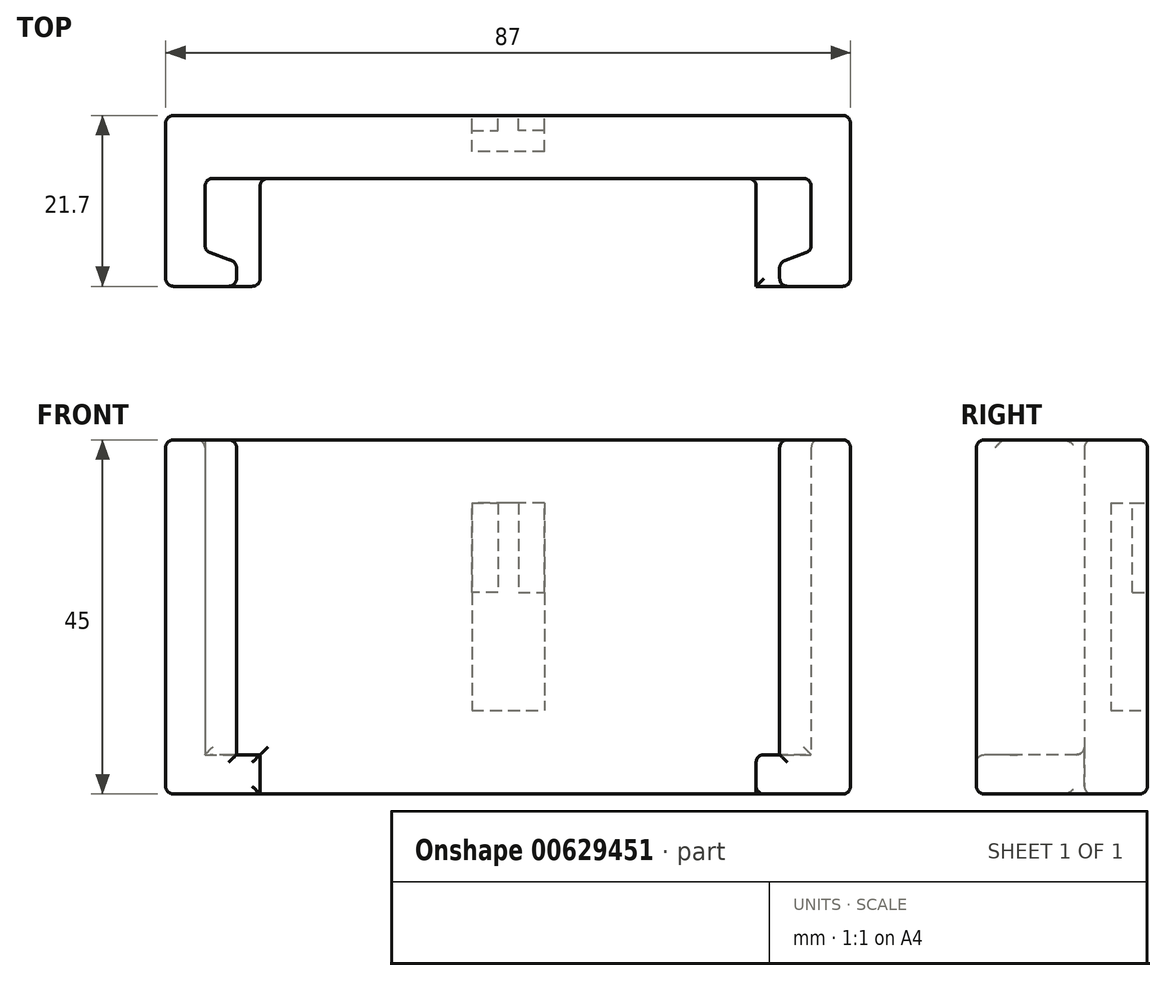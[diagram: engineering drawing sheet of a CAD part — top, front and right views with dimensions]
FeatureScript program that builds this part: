
annotation { "Feature Type Name" : "Feature", "Feature Type Description" : "" }
export const myFeature = defineFeature(function(context is Context, id is Id, definition is map)
    precondition{}
    {
        {
            var Q0;
            Q0=qCreatedBy(makeId("Top.planeOp"),FACE);
            var sketch = newSketch(context, id + "F0", { "sketchPlane" : qUnion([Q0])});
            skLineSegment(sketch, "E0", {"start": v(0, 0) * mm, "end": v(87, 0) * mm});
            skLineSegment(sketch, "E1", {"start": v(87, 0) * mm, "end": v(87, -21.7) * mm});
            skLineSegment(sketch, "E2", {"start": v(87, -21.7) * mm, "end": v(0, -21.7) * mm});
            skLineSegment(sketch, "E3", {"start": v(0, -21.7) * mm, "end": v(0, 0) * mm});
            skSolve(sketch);
        }
        {
            var Q0;
            Q0 = qSketchRegion(id + "F0", true);
            extrude(context, id + "F1", {"entities" : qUnion([Q0]), "depth" : 5 * mm, "offsetDistance" : 25 * mm});
        }
        {
            var Q0;
            Q0=makeQuery(id+"F1.opExtrude","CAP_FACE",FACE,{"disambiguationData":[OSD([sQuery(id+"F0.wireOp",EDGE,"E0"),sQuery(id+"F0.wireOp",EDGE,"E1"),sQuery(id+"F0.wireOp",EDGE,"E2"),sQuery(id+"F0.wireOp",EDGE,"E3")])],"isStart":false});
            var sketch = newSketch(context, id + "F2", { "sketchPlane" : qUnion([Q0])});
            skLineSegment(sketch, "E4", {"start": v(0, 0) * mm, "end": v(0, -21.7) * mm});
            skLineSegment(sketch, "E5", {"start": v(0, -21.7) * mm, "end": v(9, -21.7) * mm});
            skLineSegment(sketch, "E6", {"start": v(9, -21.7) * mm, "end": v(9, -18.66) * mm});
            skLineSegment(sketch, "E7", {"start": v(9, -18.66) * mm, "end": v(5, -17.2) * mm});
            skLineSegment(sketch, "E8", {"start": v(5, -17.2) * mm, "end": v(5, -8) * mm});
            skLineSegment(sketch, "E9", {"start": v(5, -8) * mm, "end": v(82, -8) * mm});
            skLineSegment(sketch, "E10", {"start": v(82, -8) * mm, "end": v(82, -17.2) * mm});
            skLineSegment(sketch, "E11", {"start": v(82, -17.2) * mm, "end": v(78, -18.66) * mm});
            skLineSegment(sketch, "E12", {"start": v(78, -18.66) * mm, "end": v(78, -21.7) * mm});
            skLineSegment(sketch, "E13", {"start": v(78, -21.7) * mm, "end": v(87, -21.7) * mm});
            skLineSegment(sketch, "E14", {"start": v(87, -21.7) * mm, "end": v(87, 0) * mm});
            skLineSegment(sketch, "E15", {"start": v(87, 0) * mm, "end": v(0, 0) * mm});
            skSolve(sketch);
        }
        {
            var Q0;
            Q0=makeQuery(id+"F2.imprint","IMPRINT",FACE,{"disambiguationData":[TD([[makeQuery(id+"F2.imprint","IMPRINT",EDGE,{"derivedFrom":sQuery(id+"F2.wireOp",EDGE,"E4")}),-1.0]])]});
            extrude(context, id + "F3", {"entities" : qUnion([Q0]), "operationType" : NewBodyOperationType.ADD, "depth" : 40 * mm, "offsetDistance" : 25 * mm});
        }
        {
            var Q0;
            Q0=makeQuery(id+"F3.boolean.opBoolean","MERGE",FACE,{"derivedFrom":[makeQuery(id+"F1.opExtrude","SWEPT_FACE",FACE,{"disambiguationData":[OSD([sQuery(id+"F0.wireOp",EDGE,"E0")])]}),makeQuery(id+"F3.opExtrude","SWEPT_FACE",FACE,{"disambiguationData":[OSD([sQuery(id+"F2.wireOp",EDGE,"E15")])]})]});
            var sketch = newSketch(context, id + "F4", { "sketchPlane" : qUnion([Q0])});
            skLineSegment(sketch, "E16", {"start": v(-43.5, 45) * mm, "end": v(-43.5, 0) * mm, "construction": true});
            skLineSegment(sketch, "E17", {"start": v(-43.5, 37) * mm, "end": v(-44.8, 37) * mm});
            skLineSegment(sketch, "E18", {"start": v(-44.8, 37) * mm, "end": v(-44.8, 25.6) * mm});
            skLineSegment(sketch, "E19", {"start": v(-44.8, 25.6) * mm, "end": v(-48.1, 25.6) * mm});
            skLineSegment(sketch, "E20", {"start": v(-48.1, 25.6) * mm, "end": v(-48.1, 10.6) * mm});
            skLineSegment(sketch, "E21", {"start": v(-48.1, 10.6) * mm, "end": v(-43.5, 10.6) * mm});
            skLineSegment(sketch, "E22", {"start": v(-43.5, 10.6) * mm, "end": v(-43.5, 37) * mm});
            skLineSegment(sketch, "E23", {"start": v(-43.5, 37) * mm, "end": v(-42.2, 37) * mm});
            skLineSegment(sketch, "E24", {"start": v(-42.2, 37) * mm, "end": v(-42.2, 25.6) * mm});
            skLineSegment(sketch, "E25", {"start": v(-42.2, 25.6) * mm, "end": v(-38.9, 25.6) * mm});
            skLineSegment(sketch, "E26", {"start": v(-38.9, 25.6) * mm, "end": v(-38.9, 10.6) * mm});
            skLineSegment(sketch, "E27", {"start": v(-38.9, 10.6) * mm, "end": v(-43.5, 10.6) * mm});
            skSolve(sketch);
        }
        {
            var Q0;
            Q0=makeQuery(id+"F4.imprint","IMPRINT",FACE,{"disambiguationData":[TD([[makeQuery(id+"F4.imprint","IMPRINT",EDGE,{"derivedFrom":sQuery(id+"F4.wireOp",EDGE,"E22")}),-1.0]])]});
            var Q1;
            Q1=makeQuery(id+"F4.imprint","IMPRINT",FACE,{"disambiguationData":[TD([[makeQuery(id+"F4.imprint","IMPRINT",EDGE,{"derivedFrom":sQuery(id+"F4.wireOp",EDGE,"E17")}),1.0]])]});
            extrude(context, id + "F5", {"entities" : qUnion([Q0, Q1]), "operationType" : NewBodyOperationType.REMOVE, "oppositeDirection" : true, "depth" : 4.6 * mm, "offsetDistance" : 25 * mm});
        }
        {
            var Q0;
            Q0=makeQuery(id+"F5.boolean.opBoolean","COPY",FACE,{"derivedFrom":makeQuery(id+"F5.opExtrude","SWEPT_FACE",FACE,{"disambiguationData":[OSD([sQuery(id+"F4.wireOp",EDGE,"E24")])]})});
            var sketch = newSketch(context, id + "F6", { "sketchPlane" : qUnion([Q0])});
            skLineSegment(sketch, "E28", {"start": v(-1.9, 37) * mm, "end": v(0, 37) * mm});
            skLineSegment(sketch, "E29", {"start": v(0, 37) * mm, "end": v(0, 25.6) * mm});
            skLineSegment(sketch, "E30", {"start": v(0, 25.6) * mm, "end": v(-1.9, 25.6) * mm});
            skLineSegment(sketch, "E31", {"start": v(-1.9, 25.6) * mm, "end": v(-1.9, 37) * mm});
            skLineSegment(sketch, "E32.bottom", {"start": v(-1.9, 25.6) * mm, "end": v(-4.6, 25.6) * mm});
            skLineSegment(sketch, "E32.top", {"start": v(-1.9, 37) * mm, "end": v(-4.6, 37) * mm});
            skLineSegment(sketch, "E32.right", {"start": v(-4.6, 25.6) * mm, "end": v(-4.6, 37) * mm});
            skSolve(sketch);
        }
        {
            var Q0;
            Q0=makeQuery(id+"F6.imprint","IMPRINT",FACE,{"disambiguationData":[TD([[makeQuery(id+"F6.imprint","IMPRINT",EDGE,{"derivedFrom":sQuery(id+"F6.wireOp",EDGE,"E32.bottom")}),1.0]])]});
            extrude(context, id + "F7", {"entities" : qUnion([Q0]), "operationType" : NewBodyOperationType.REMOVE, "oppositeDirection" : true, "depth" : 3.3 * mm, "offsetDistance" : 25 * mm});
        }
        {
            var Q0;
            Q0=makeQuery(id+"F5.boolean.opBoolean","COPY",FACE,{"derivedFrom":makeQuery(id+"F5.opExtrude","SWEPT_FACE",FACE,{"disambiguationData":[OSD([sQuery(id+"F4.wireOp",EDGE,"E18")])]})});
            var sketch = newSketch(context, id + "F8", { "sketchPlane" : qUnion([Q0])});
            skLineSegment(sketch, "E33", {"start": v(1.9, 37) * mm, "end": v(0, 37) * mm});
            skLineSegment(sketch, "E34", {"start": v(0, 37) * mm, "end": v(0, 25.6) * mm});
            skLineSegment(sketch, "E35", {"start": v(0, 25.6) * mm, "end": v(1.9, 25.6) * mm});
            skLineSegment(sketch, "E36", {"start": v(1.9, 25.6) * mm, "end": v(1.9, 37) * mm});
            skLineSegment(sketch, "E37.bottom", {"start": v(4.6, 37) * mm, "end": v(1.9, 37) * mm});
            skLineSegment(sketch, "E37.top", {"start": v(4.6, 25.6) * mm, "end": v(1.9, 25.6) * mm});
            skLineSegment(sketch, "E37.left", {"start": v(4.6, 37) * mm, "end": v(4.6, 25.6) * mm});
            skLineSegment(sketch, "E37.right", {"start": v(1.9, 37) * mm, "end": v(1.9, 25.6) * mm});
            skSolve(sketch);
        }
        {
            var Q0;
            Q0=makeQuery(id+"F8.imprint","IMPRINT",FACE,{"disambiguationData":[TD([[makeQuery(id+"F8.imprint","IMPRINT",EDGE,{"derivedFrom":sQuery(id+"F8.wireOp",EDGE,"E37.bottom")}),1.0]])]});
            extrude(context, id + "F9", {"entities" : qUnion([Q0]), "operationType" : NewBodyOperationType.REMOVE, "oppositeDirection" : true, "depth" : 3.3 * mm, "offsetDistance" : 25 * mm});
        }
        {
            var Q0;
            Q0=makeQuery(id+"F3.boolean.opBoolean","MERGE",FACE,{"derivedFrom":[makeQuery(id+"F1.opExtrude","SWEPT_FACE",FACE,{"disambiguationData":[OSD([sQuery(id+"F0.wireOp",EDGE,"E2")])]}),makeQuery(id+"F3.opExtrude","SWEPT_FACE",FACE,{"disambiguationData":[OSD([sQuery(id+"F2.wireOp",EDGE,"E5")])]}),makeQuery(id+"F3.opExtrude","SWEPT_FACE",FACE,{"disambiguationData":[OSD([sQuery(id+"F2.wireOp",EDGE,"E13")])]})]});
            var sketch = newSketch(context, id + "F10", { "sketchPlane" : qUnion([Q0])});
            skLineSegment(sketch, "E38", {"start": v(12, 5) * mm, "end": v(12, 0) * mm});
            skLineSegment(sketch, "E39", {"start": v(12, 0) * mm, "end": v(75, 0) * mm});
            skLineSegment(sketch, "E40", {"start": v(75, 0) * mm, "end": v(75, 5) * mm});
            skLineSegment(sketch, "E41", {"start": v(75, 5) * mm, "end": v(12, 5) * mm});
            skSolve(sketch);
        }
        {
            var Q0;
            Q0=makeQuery(id+"F10.imprint","IMPRINT",FACE,{"disambiguationData":[TD([[makeQuery(id+"F10.imprint","IMPRINT",EDGE,{"derivedFrom":sQuery(id+"F10.wireOp",EDGE,"E38")}),1.0]])]});
            extrude(context, id + "F11", {"entities" : qUnion([Q0]), "operationType" : NewBodyOperationType.REMOVE, "oppositeDirection" : true, "depth" : 13.7 * mm, "offsetDistance" : 25 * mm});
        }
        {
            var Q0;
            Q0=makeQuery(id+"F11.boolean.opBoolean","COPY",EDGE,{"derivedFrom":makeQuery(id+"F11.opExtrude","SWEPT_EDGE",EDGE,{"disambiguationData":[OSD([sQuery(id+"F0.wireOp",EDGE,"E2"),sQuery(id+"F10.wireOp",EDGE,"E38"),sQuery(id+"F10.wireOp",EDGE,"E41")])]})});
            var Q1;
            Q1=makeQuery(id+"F11.boolean.opBoolean","COPY",EDGE,{"derivedFrom":makeQuery(id+"F11.opExtrude","SWEPT_EDGE",EDGE,{"disambiguationData":[OSD([sQuery(id+"F0.wireOp",EDGE,"E2"),sQuery(id+"F10.wireOp",EDGE,"E38"),sQuery(id+"F10.wireOp",EDGE,"E39")])]})});
            var Q2;
            Q2=makeQuery(id+"F11.boolean.opBoolean","COPY",EDGE,{"derivedFrom":makeQuery(id+"F11.opExtrude","CAP_EDGE",EDGE,{"disambiguationData":[OSD([sQuery(id+"F10.wireOp",EDGE,"E38")])],"isStart":false})});
            var Q3;
            Q3=makeQuery(id+"F11.boolean.opBoolean","COPY",EDGE,{"derivedFrom":makeQuery(id+"F11.opExtrude","CAP_EDGE",EDGE,{"disambiguationData":[OSD([sQuery(id+"F10.wireOp",EDGE,"E39")])],"isStart":false})});
            var Q4;
            Q4=makeQuery(id+"F3.opExtrude","SWEPT_EDGE",EDGE,{"disambiguationData":[OSD([sQuery(id+"F2.wireOp",EDGE,"E8"),sQuery(id+"F2.wireOp",EDGE,"E9")])]});
            var Q5;
            Q5=makeQuery(id+"F3.opExtrude","CAP_EDGE",EDGE,{"disambiguationData":[OSD([sQuery(id+"F2.wireOp",EDGE,"E8")])],"isStart":true});
            var Q6;
            Q6=makeQuery(id+"F3.opExtrude","SWEPT_EDGE",EDGE,{"disambiguationData":[OSD([sQuery(id+"F2.wireOp",EDGE,"E6"),sQuery(id+"F2.wireOp",EDGE,"E7")])]});
            var Q7;
            Q7=makeQuery(id+"F3.opExtrude","SWEPT_EDGE",EDGE,{"disambiguationData":[OSD([sQuery(id+"F0.wireOp",EDGE,"E2"),sQuery(id+"F2.wireOp",EDGE,"E5"),sQuery(id+"F2.wireOp",EDGE,"E6")])]});
            var Q8;
            {var subQ0=sQuery(id+"F0.wireOp",EDGE,"E2");Q8=makeQuery(id+"F11.boolean.opBoolean","SPLIT",EDGE,{"disambiguationData":[TD([makeQuery(id+"F3.opExtrude","SWEPT_FACE",FACE,{"disambiguationData":[OSD([sQuery(id+"F2.wireOp",EDGE,"E6")])]})])],"derivedFrom":makeQuery(id+"F1.opExtrude","CAP_EDGE",EDGE,{"disambiguationData":[OSD([subQ0])],"isStart":false})});}
            var Q9;
            Q9=makeQuery(id+"F3.opExtrude","CAP_EDGE",EDGE,{"disambiguationData":[OSD([sQuery(id+"F2.wireOp",EDGE,"E6")])],"isStart":true});
            var Q10;
            {var subQ0=sQuery(id+"F0.wireOp",EDGE,"E3");var subQ1=sQuery(id+"F0.wireOp",EDGE,"E2");Q10=makeQuery(id+"F11.boolean.opBoolean","SPLIT",EDGE,{"disambiguationData":[TD([makeQuery(id+"F1.opExtrude","SWEPT_FACE",FACE,{"disambiguationData":[OSD([subQ0])]})])],"derivedFrom":makeQuery(id+"F1.opExtrude","CAP_EDGE",EDGE,{"disambiguationData":[OSD([subQ1])],"isStart":true})});}
            var Q11;
            Q11=makeQuery(id+"F3.boolean.opBoolean","MERGE",EDGE,{"derivedFrom":[makeQuery(id+"F1.opExtrude","SWEPT_EDGE",EDGE,{"disambiguationData":[OSD([sQuery(id+"F0.wireOp",EDGE,"E2"),sQuery(id+"F0.wireOp",EDGE,"E3")])]}),makeQuery(id+"F3.opExtrude","SWEPT_EDGE",EDGE,{"disambiguationData":[OSD([sQuery(id+"F2.wireOp",EDGE,"E4"),sQuery(id+"F2.wireOp",EDGE,"E5")])]})]});
            var Q12;
            Q12=makeQuery(id+"F3.opExtrude","CAP_EDGE",EDGE,{"disambiguationData":[OSD([sQuery(id+"F2.wireOp",EDGE,"E9")])],"isStart":false});
            var Q13;
            Q13=makeQuery(id+"F3.opExtrude","CAP_EDGE",EDGE,{"disambiguationData":[OSD([sQuery(id+"F2.wireOp",EDGE,"E10")])],"isStart":false});
            var Q14;
            Q14=makeQuery(id+"F3.opExtrude","CAP_EDGE",EDGE,{"disambiguationData":[OSD([sQuery(id+"F2.wireOp",EDGE,"E11")])],"isStart":false});
            var Q15;
            Q15=makeQuery(id+"F3.opExtrude","CAP_EDGE",EDGE,{"disambiguationData":[OSD([sQuery(id+"F2.wireOp",EDGE,"E12")])],"isStart":false});
            var Q16;
            Q16=makeQuery(id+"F3.opExtrude","CAP_EDGE",EDGE,{"disambiguationData":[OSD([sQuery(id+"F2.wireOp",EDGE,"E13")])],"isStart":false});
            var Q17;
            Q17=makeQuery(id+"F3.opExtrude","CAP_EDGE",EDGE,{"disambiguationData":[OSD([sQuery(id+"F2.wireOp",EDGE,"E14")])],"isStart":false});
            var Q18;
            Q18=makeQuery(id+"F3.boolean.opBoolean","MERGE",EDGE,{"derivedFrom":[makeQuery(id+"F1.opExtrude","SWEPT_EDGE",EDGE,{"disambiguationData":[OSD([sQuery(id+"F0.wireOp",EDGE,"E1"),sQuery(id+"F0.wireOp",EDGE,"E2")])]}),makeQuery(id+"F3.opExtrude","SWEPT_EDGE",EDGE,{"disambiguationData":[OSD([sQuery(id+"F2.wireOp",EDGE,"E13"),sQuery(id+"F2.wireOp",EDGE,"E14")])]})]});
            var Q19;
            Q19=makeQuery(id+"F11.boolean.opBoolean","MERGE",FACE,{"derivedFrom":[makeQuery(id+"F3.opExtrude","SWEPT_FACE",FACE,{"disambiguationData":[OSD([sQuery(id+"F2.wireOp",EDGE,"E9")])]}),makeQuery(id+"F11.opExtrude","CAP_FACE",FACE,{"disambiguationData":[OSD([sQuery(id+"F10.wireOp",EDGE,"E38"),sQuery(id+"F10.wireOp",EDGE,"E39"),sQuery(id+"F10.wireOp",EDGE,"E40"),sQuery(id+"F10.wireOp",EDGE,"E41")])],"isStart":false})]});
            var Q20;
            Q20=makeQuery(id+"F3.opExtrude","SWEPT_EDGE",EDGE,{"disambiguationData":[OSD([sQuery(id+"F0.wireOp",EDGE,"E2"),sQuery(id+"F2.wireOp",EDGE,"E12"),sQuery(id+"F2.wireOp",EDGE,"E13")])]});
            var Q21;
            Q21=makeQuery(id+"F11.boolean.opBoolean","COPY",EDGE,{"derivedFrom":makeQuery(id+"F11.opExtrude","SWEPT_EDGE",EDGE,{"disambiguationData":[OSD([sQuery(id+"F0.wireOp",EDGE,"E2"),sQuery(id+"F10.wireOp",EDGE,"E40"),sQuery(id+"F10.wireOp",EDGE,"E41")])]})});
            var Q22;
            Q22=makeQuery(id+"F3.opExtrude","CAP_EDGE",EDGE,{"disambiguationData":[OSD([sQuery(id+"F2.wireOp",EDGE,"E10")])],"isStart":true});
            var Q23;
            {var subQ0=sQuery(id+"F0.wireOp",EDGE,"E2");Q23=makeQuery(id+"F11.boolean.opBoolean","SPLIT",EDGE,{"disambiguationData":[TD([makeQuery(id+"F3.opExtrude","SWEPT_FACE",FACE,{"disambiguationData":[OSD([sQuery(id+"F2.wireOp",EDGE,"E12")])]})])],"derivedFrom":makeQuery(id+"F1.opExtrude","CAP_EDGE",EDGE,{"disambiguationData":[OSD([subQ0])],"isStart":false})});}
            var Q24;
            Q24=makeQuery(id+"F3.opExtrude","CAP_EDGE",EDGE,{"disambiguationData":[OSD([sQuery(id+"F2.wireOp",EDGE,"E12")])],"isStart":true});
            var Q25;
            Q25=makeQuery(id+"F3.opExtrude","SWEPT_EDGE",EDGE,{"disambiguationData":[OSD([sQuery(id+"F2.wireOp",EDGE,"E11"),sQuery(id+"F2.wireOp",EDGE,"E12")])]});
            var Q26;
            Q26=makeQuery(id+"F3.opExtrude","SWEPT_EDGE",EDGE,{"disambiguationData":[OSD([sQuery(id+"F2.wireOp",EDGE,"E10"),sQuery(id+"F2.wireOp",EDGE,"E11")])]});
            var Q27;
            Q27=makeQuery(id+"F3.opExtrude","SWEPT_EDGE",EDGE,{"disambiguationData":[OSD([sQuery(id+"F2.wireOp",EDGE,"E7"),sQuery(id+"F2.wireOp",EDGE,"E8")])]});
            var Q28;
            Q28=makeQuery(id+"F3.opExtrude","CAP_EDGE",EDGE,{"disambiguationData":[OSD([sQuery(id+"F2.wireOp",EDGE,"E5")])],"isStart":false});
            var Q29;
            Q29=makeQuery(id+"F3.opExtrude","CAP_EDGE",EDGE,{"disambiguationData":[OSD([sQuery(id+"F2.wireOp",EDGE,"E6")])],"isStart":false});
            var Q30;
            Q30=makeQuery(id+"F3.opExtrude","CAP_EDGE",EDGE,{"disambiguationData":[OSD([sQuery(id+"F2.wireOp",EDGE,"E4")])],"isStart":false});
            var Q31;
            Q31=makeQuery(id+"F3.opExtrude","CAP_EDGE",EDGE,{"disambiguationData":[OSD([sQuery(id+"F2.wireOp",EDGE,"E15")])],"isStart":false});
            var Q32;
            Q32=makeQuery(id+"F3.boolean.opBoolean","MERGE",EDGE,{"derivedFrom":[makeQuery(id+"F1.opExtrude","SWEPT_EDGE",EDGE,{"disambiguationData":[OSD([sQuery(id+"F0.wireOp",EDGE,"E0"),sQuery(id+"F0.wireOp",EDGE,"E1")])]}),makeQuery(id+"F3.opExtrude","SWEPT_EDGE",EDGE,{"disambiguationData":[OSD([sQuery(id+"F2.wireOp",EDGE,"E14"),sQuery(id+"F2.wireOp",EDGE,"E15")])]})]});
            var Q33;
            Q33=makeQuery(id+"F1.opExtrude","CAP_EDGE",EDGE,{"disambiguationData":[OSD([sQuery(id+"F0.wireOp",EDGE,"E1")])],"isStart":true});
            var Q34;
            {var subQ0=sQuery(id+"F0.wireOp",EDGE,"E2");var subQ1=sQuery(id+"F0.wireOp",EDGE,"E1");Q34=makeQuery(id+"F11.boolean.opBoolean","SPLIT",EDGE,{"disambiguationData":[TD([makeQuery(id+"F1.opExtrude","SWEPT_FACE",FACE,{"disambiguationData":[OSD([subQ1])]})])],"derivedFrom":makeQuery(id+"F1.opExtrude","CAP_EDGE",EDGE,{"disambiguationData":[OSD([subQ0])],"isStart":true})});}
            var Q35;
            Q35=makeQuery(id+"F11.boolean.opBoolean","COPY",EDGE,{"derivedFrom":makeQuery(id+"F11.opExtrude","CAP_EDGE",EDGE,{"disambiguationData":[OSD([sQuery(id+"F10.wireOp",EDGE,"E40")])],"isStart":true})});
            var Q36;
            Q36=makeQuery(id+"F11.boolean.opBoolean","COPY",EDGE,{"derivedFrom":makeQuery(id+"F11.opExtrude","CAP_EDGE",EDGE,{"disambiguationData":[OSD([sQuery(id+"F10.wireOp",EDGE,"E38")])],"isStart":true})});
            var Q37;
            Q37=makeQuery(id+"F1.opExtrude","CAP_EDGE",EDGE,{"disambiguationData":[OSD([sQuery(id+"F0.wireOp",EDGE,"E0")])],"isStart":true});
            var Q38;
            Q38=makeQuery(id+"F3.boolean.opBoolean","MERGE",EDGE,{"derivedFrom":[makeQuery(id+"F1.opExtrude","SWEPT_EDGE",EDGE,{"disambiguationData":[OSD([sQuery(id+"F0.wireOp",EDGE,"E0"),sQuery(id+"F0.wireOp",EDGE,"E3")])]}),makeQuery(id+"F3.opExtrude","SWEPT_EDGE",EDGE,{"disambiguationData":[OSD([sQuery(id+"F2.wireOp",EDGE,"E4"),sQuery(id+"F2.wireOp",EDGE,"E15")])]})]});
            var Q39;
            Q39=makeQuery(id+"F1.opExtrude","CAP_EDGE",EDGE,{"disambiguationData":[OSD([sQuery(id+"F0.wireOp",EDGE,"E3")])],"isStart":true});
            var Q40;
            Q40=makeQuery(id+"F11.boolean.opBoolean","COPY",EDGE,{"derivedFrom":makeQuery(id+"F11.opExtrude","SWEPT_EDGE",EDGE,{"disambiguationData":[OSD([sQuery(id+"F0.wireOp",EDGE,"E2"),sQuery(id+"F10.wireOp",EDGE,"E39"),sQuery(id+"F10.wireOp",EDGE,"E40")])]})});
            fillet(context, id + "F12", {"entities" : qUnion([Q0, Q1, Q2, Q3, Q4, Q5, Q6, Q7, Q8, Q9, Q10, Q11, Q12, Q13, Q14, Q15, Q16, Q17, Q18, Q19, Q20, Q21, Q22, Q23, Q24, Q25, Q26, Q27, Q28, Q29, Q30, Q31, Q32, Q33, Q34, Q35, Q36, Q37, Q38, Q39, Q40]), "radius" : 1 * mm, "tangentPropagation" : true, "allowEdgeOverflow" : false});
        }
    });
